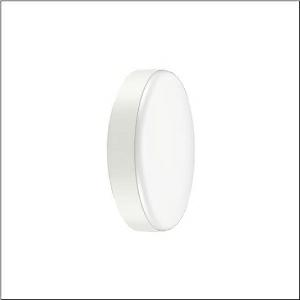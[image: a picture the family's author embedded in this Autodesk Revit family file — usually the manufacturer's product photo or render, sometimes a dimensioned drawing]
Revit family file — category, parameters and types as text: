
# Revit family: round_31_51wc10db34as
name_source: partatom
category: Lighting Fixtures
units: mm (PartAtom-declared; Revit-internal decimal feet)

## family parameters
Cut with Voids When Loaded = No
Host = Face
Light Source = No
Part Type = Normal
Room Calculation Point = No
Round Connector Dimension = Use Diameter
Shared = No

## types (1)
- Round 31 (1 x LED, 4250 lm, 35.4 W, 3000K)
    Apparent Load = 35 VA
    CIE Flux Codes = 44 75 94 94 100
    Color Rendering = 80
    Color Temperature = 3000K
    Default Elevation = 1800 mm
    Description = Round 31, wall and ceiling luminaire, primary optical cover: cover, of PC, opal, light emission: direct distribution, primary light characteristic: symmetric, installation type: surface-mounted, LED, rated luminous flux: 4.250lm, luminous efficacy: 120lm/W, light colour: 830, colour temperature: 3000K, control gear: DALI 2, with terminal, 5-pole, max. 2.5mm², mains connection: 220..240V, AC, 50/60Hz, rated input power: 35.5W, luminaire housing, of PC, traffic white (RAL 9016), diameter: 480mm, brightness and presence sensor, HF sensor, protection rating (complete): IP65, insulation class (complete): insulation class II (safety insulation), certification: CE, impact resistance: IK10, permissible operating ambient temperature: -20..+40°C, permissible storage temperature: -20..+60°C, packaging unit: 1 piece
    Height = 97 mm
    Lamp = 1 x LED
    Lamp Light Flux = 4250 lm
    Lamp Power = 35.4 W
    Lamp count = 1
    Length = 480 mm
    Luminous efficacy = 120 lm/W
    Manufacturer = Siteco
    ModVariant = No
    Model = 51WC10DB34AS
    Mounting Place = Ceiling
    Mounting Type = Surface mounted
    Number of Poles = 1
    OnlyDefault = Yes
    Power Factor = 1
    Product Name = Round 31
    Product group = wall and ceiling luminaire | ceiling mounted
    ProductGroupID = 305
    Protection Class = Protection class II
    Protection Degree = IP 65
    RLX_Detail_Level = 1
    RLX_Emergency_Light_Flux = 0 lm
    RLX_Emergency_Type = 0
    RLX_Emergency_Type_DB = No
    RlxData = <blob elided: 40933 chars, md5=cc1fe6f9>
    Socket = socket
    Standby Power = 0 W
    System Light Flux = 4250 lm
    System Power = 35 W
    Type Comments = Product without accessories
    Type Image = l_1007188.jpg
    URL = http://relux.com
    VarID = ---
    Voltage = 0 V
    Weight = 0.00 kg
    Width = 0 mm  [stored 0 ft]

note: [stored X ft] marks values corroborated as IEEE doubles in the binary element streams (Revit-internal decimal feet)

## geometry (parser evidence)
native form markers: Blend x4, Sweep x10
no freeform markers — native parametric forms only
